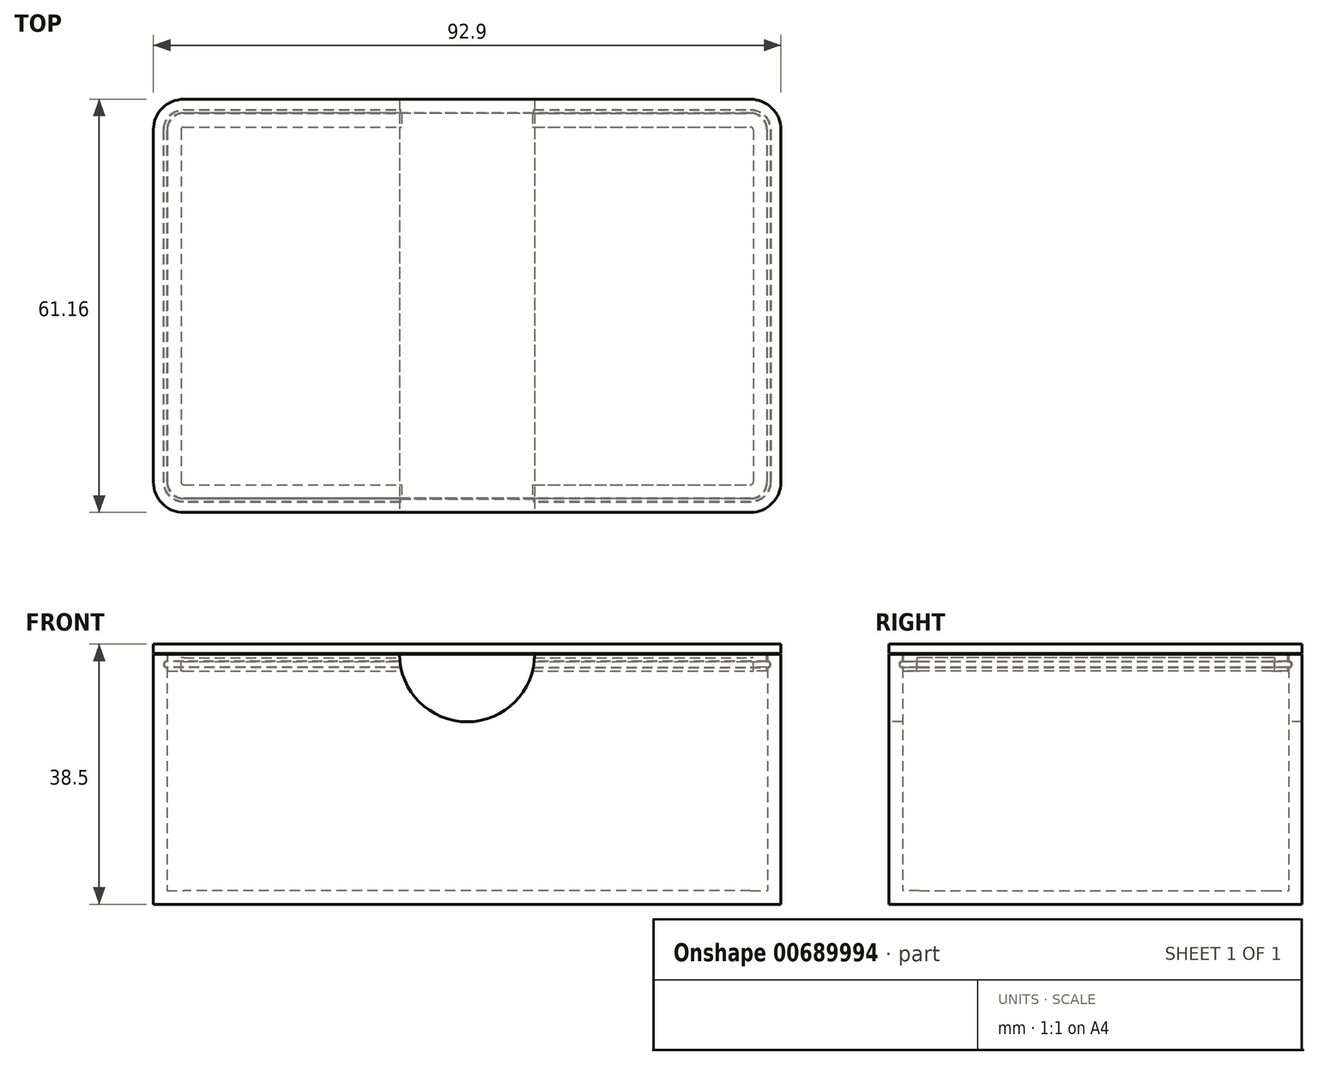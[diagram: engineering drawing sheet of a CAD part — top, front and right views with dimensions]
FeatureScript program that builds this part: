
annotation { "Feature Type Name" : "Feature", "Feature Type Description" : "" }
export const myFeature = defineFeature(function(context is Context, id is Id, definition is map)
    precondition{}
    {
        {
            assignVariable(context, id + "F0", {"name" : "thick", "anyValue" : 35 * mm});
        }
        {
            assignVariable(context, id + "F1", {"name" : "wall", "anyValue" : 2 * mm});
        }
        {
            var Q0;
            Q0=qCreatedBy(makeId("Top.planeOp"),FACE);
            var sketch = newSketch(context, id + "F2", { "sketchPlane" : qUnion([Q0])});
            skLineSegment(sketch, "E0.bottom", {"start": v(41.95, -28.57) * mm, "end": v(-41.95, -28.58) * mm});
            skLineSegment(sketch, "E0.top", {"start": v(41.95, 28.58) * mm, "end": v(-41.95, 28.57) * mm});
            skLineSegment(sketch, "E0.left", {"start": v(44.45, -26.07) * mm, "end": v(44.45, 26.08) * mm});
            skLineSegment(sketch, "E0.right", {"start": v(-44.45, -26.08) * mm, "end": v(-44.45, 26.07) * mm});
            skPoint(sketch, "E0.middle", {"position": v(0, 0) * mm});
            skPoint(sketch, "E1.visualSharp", {"position": v(-44.45, 28.57) * mm});
            skArc(sketch, "E1.filletArc", {"start": v(-41.95, 28.57) * mm, "mid": v(-43.72, 27.84) * mm, "end": v(-44.45, 26.07) * mm});
            skPoint(sketch, "E2.visualSharp", {"position": v(-44.45, -28.58) * mm});
            skArc(sketch, "E2.filletArc", {"start": v(-44.45, -26.08) * mm, "mid": v(-43.72, -27.84) * mm, "end": v(-41.95, -28.58) * mm});
            skPoint(sketch, "E3.visualSharp", {"position": v(44.45, -28.57) * mm});
            skArc(sketch, "E3.filletArc", {"start": v(41.95, -28.57) * mm, "mid": v(43.72, -27.84) * mm, "end": v(44.45, -26.07) * mm});
            skPoint(sketch, "E4.visualSharp", {"position": v(44.45, 28.58) * mm});
            skArc(sketch, "E4.filletArc", {"start": v(44.45, 26.08) * mm, "mid": v(43.72, 27.84) * mm, "end": v(41.95, 28.57) * mm});
            skSolve(sketch);
        }
        {
            var Q0;
            Q0=makeQuery(id+"F2.imprint","IMPRINT",FACE,{"disambiguationData":[TD([[makeQuery(id+"F2.imprint","IMPRINT",EDGE,{"derivedFrom":sQuery(id+"F2.wireOp",EDGE,"E0.bottom")}),-1.0]])]});
            extrude(context, id + "F3", {"entities" : qUnion([Q0]), "depth" : getVariable(context, 'thick'), "offsetDistance" : 25 * mm});
        }
        {
            var Q0;
            Q0=makeQuery(id+"F3.opExtrude","CAP_FACE",FACE,{"disambiguationData":[OSD([sQuery(id+"F2.wireOp",EDGE,"E0.bottom"),sQuery(id+"F2.wireOp",EDGE,"E0.top"),sQuery(id+"F2.wireOp",EDGE,"E0.left"),sQuery(id+"F2.wireOp",EDGE,"E0.right"),sQuery(id+"F2.wireOp",EDGE,"E1.filletArc"),sQuery(id+"F2.wireOp",EDGE,"E2.filletArc"),sQuery(id+"F2.wireOp",EDGE,"E3.filletArc"),sQuery(id+"F2.wireOp",EDGE,"E4.filletArc")])],"isStart":false});
            shell(context, id + "F4", {"entities" : qUnion([Q0]), "thickness" : getVariable(context, 'wall'), "oppositeDirection" : true});
        }
        {
            var Q0;
            Q0=makeQuery(id+"F3.opExtrude","CAP_FACE",FACE,{"disambiguationData":[OSD([sQuery(id+"F2.wireOp",EDGE,"E0.bottom"),sQuery(id+"F2.wireOp",EDGE,"E0.top"),sQuery(id+"F2.wireOp",EDGE,"E0.left"),sQuery(id+"F2.wireOp",EDGE,"E0.right"),sQuery(id+"F2.wireOp",EDGE,"E1.filletArc"),sQuery(id+"F2.wireOp",EDGE,"E2.filletArc"),sQuery(id+"F2.wireOp",EDGE,"E3.filletArc"),sQuery(id+"F2.wireOp",EDGE,"E4.filletArc")])],"isStart":false});
            cPlane(context, id + "F5", {"entities" : qUnion([Q0]), "cplaneType" : CPlaneType.OFFSET, "offset" : 1.5 * mm, "oppositeDirection" : true, "width" : 150 * mm, "height" : 150 * mm});
        }
        {
            var Q0;
            Q0=qCreatedBy(id+"F5.planeOp",FACE);
            var sketch = newSketch(context, id + "F6", { "sketchPlane" : qUnion([Q0])});
            skLineSegment(sketch, "E5.0", {"start": v(44.45, -26.07) * mm, "end": v(44.45, 26.08) * mm});
            skArc(sketch, "E5.1", {"start": v(41.95, -28.57) * mm, "mid": v(43.72, -27.84) * mm, "end": v(44.45, -26.07) * mm});
            skArc(sketch, "E5.2", {"start": v(44.45, 26.08) * mm, "mid": v(43.72, 27.84) * mm, "end": v(41.95, 28.57) * mm});
            skLineSegment(sketch, "E5.3", {"start": v(-41.95, -28.58) * mm, "end": v(41.95, -28.57) * mm});
            skLineSegment(sketch, "E5.4", {"start": v(41.95, 28.58) * mm, "end": v(-41.95, 28.57) * mm});
            skArc(sketch, "E5.5", {"start": v(-41.95, 28.57) * mm, "mid": v(-43.72, 27.84) * mm, "end": v(-44.45, 26.07) * mm});
            skLineSegment(sketch, "E5.6", {"start": v(-44.45, 26.07) * mm, "end": v(-44.45, -26.08) * mm});
            skArc(sketch, "E5.7", {"start": v(-44.45, -26.08) * mm, "mid": v(-43.72, -27.84) * mm, "end": v(-41.95, -28.58) * mm});
            skSolve(sketch);
        }
        {
            var Q0;
            Q0=qCreatedBy(makeId("Right.planeOp"),FACE);
            var sketch = newSketch(context, id + "F7", { "sketchPlane" : qUnion([Q0])});
            skCircle(sketch, "E6", {"center": v(28.57, 33.5) * mm, "radius": 0.5 * mm});
            skSolve(sketch);
        }
        {
            var Q0;
            Q0 = qSketchRegion(id + "F7", true);
            var Q1;
            Q1 = qConstructionFilter(qBodyType(qCreatedBy(id + "F6" ,EDGE), BodyType.WIRE), ConstructionObject.NO);
            sweep(context, id + "F8", {"operationType" : NewBodyOperationType.REMOVE, "profiles" : qUnion([Q0]), "path" : qUnion([Q1])});
        }
        {
            var Q0;
            Q0=qCreatedBy(id+"F5.planeOp",FACE);
            var sketch = newSketch(context, id + "F9", { "sketchPlane" : qUnion([Q0])});
            skLineSegment(sketch, "E7.0", {"start": v(41.95, 30.58) * mm, "end": v(-41.95, 30.58) * mm});
            skArc(sketch, "E7.1", {"start": v(46.45, 26.08) * mm, "mid": v(45.13, 29.26) * mm, "end": v(41.95, 30.57) * mm});
            skArc(sketch, "E7.2", {"start": v(-41.95, 30.57) * mm, "mid": v(-45.13, 29.26) * mm, "end": v(-46.45, 26.07) * mm});
            skLineSegment(sketch, "E7.3", {"start": v(46.45, -26.07) * mm, "end": v(46.45, 26.08) * mm});
            skLineSegment(sketch, "E7.4", {"start": v(-46.45, -26.08) * mm, "end": v(-46.45, 26.07) * mm});
            skArc(sketch, "E7.5", {"start": v(-46.45, -26.08) * mm, "mid": v(-45.13, -29.26) * mm, "end": v(-41.95, -30.58) * mm});
            skLineSegment(sketch, "E7.6", {"start": v(41.95, -30.58) * mm, "end": v(-41.95, -30.58) * mm});
            skArc(sketch, "E7.7", {"start": v(41.95, -30.57) * mm, "mid": v(45.13, -29.26) * mm, "end": v(46.45, -26.07) * mm});
            skSolve(sketch);
        }
        {
            var Q0;
            Q0 = qSketchRegion(id + "F9", true);
            extrude(context, id + "F10", {"entities" : qUnion([Q0]), "depth" : 3 * mm, "offsetDistance" : 25 * mm, "hasSecondDirection" : true, "secondDirectionOppositeDirection" : true, "secondDirectionDepth" : 1 * mm});
        }
        {
            var Q0;
            Q0=makeQuery(id+"F3.opExtrude","SWEPT_BODY",BODY,{"disambiguationData":[OSD([sQuery(id+"F2.wireOp",EDGE,"E0.bottom"),sQuery(id+"F2.wireOp",EDGE,"E0.top"),sQuery(id+"F2.wireOp",EDGE,"E0.left"),sQuery(id+"F2.wireOp",EDGE,"E0.right"),sQuery(id+"F2.wireOp",EDGE,"E1.filletArc"),sQuery(id+"F2.wireOp",EDGE,"E2.filletArc"),sQuery(id+"F2.wireOp",EDGE,"E3.filletArc"),sQuery(id+"F2.wireOp",EDGE,"E4.filletArc")])]});
            var Q1;
            Q1=makeQuery(id+"F10.opExtrude","SWEPT_BODY",BODY,{"disambiguationData":[OSD([sQuery(id+"F9.wireOp",EDGE,"E7.0"),sQuery(id+"F9.wireOp",EDGE,"E7.1"),sQuery(id+"F9.wireOp",EDGE,"E7.2"),sQuery(id+"F9.wireOp",EDGE,"E7.3"),sQuery(id+"F9.wireOp",EDGE,"E7.4"),sQuery(id+"F9.wireOp",EDGE,"E7.5"),sQuery(id+"F9.wireOp",EDGE,"E7.6"),sQuery(id+"F9.wireOp",EDGE,"E7.7")])]});
            booleanBodies(context, id + "F11", {"operationType" : BooleanOperationType.SUBTRACTION, "tools" : qUnion([Q0]), "targets" : qUnion([Q1]), "offset" : true, "offsetAll" : true, "offsetDistance" : 0.1 * mm, "keepTools" : true});
        }
        {
            var Q0;
            Q0=makeQuery(id+"F3.opExtrude","SWEPT_FACE",FACE,{"disambiguationData":[OSD([sQuery(id+"F2.wireOp",EDGE,"E0.bottom")])]});
            var sketch = newSketch(context, id + "F12", { "sketchPlane" : qUnion([Q0])});
            skCircle(sketch, "E8", {"center": v(0, 35) * mm, "radius": 10 * mm});
            skSolve(sketch);
        }
        {
            var Q0;
            {var subQ0=sQuery(id+"F12.wireOp",EDGE,"E8");var subQ1=makeQuery(id+"F3.opExtrude","CAP_EDGE",EDGE,{"disambiguationData":[OSD([sQuery(id+"F2.wireOp",EDGE,"E0.bottom")])],"isStart":false});var subQ2=makeQuery(id+"F12.imprint","INTERSECT",VERTEX,{"disambiguationData":[OD(0.0)],"derivedFrom":[subQ1,subQ0]});Q0=makeQuery(id+"F12.imprint","IMPRINT",FACE,{"disambiguationData":[TD([[makeQuery(id+"F12.imprint","IMPRINT",EDGE,{"disambiguationData":[TD([[subQ2,1.0]])],"derivedFrom":subQ0}),1.0]])]});}
            extrude(context, id + "F13", {"entities" : qUnion([Q0]), "operationType" : NewBodyOperationType.REMOVE, "endBound" : BoundingType.THROUGH_ALL, "oppositeDirection" : true, "depth" : 25 * mm, "offsetDistance" : 25 * mm});
        }
        {
            var Q0;
            Q0=makeQuery(id+"F10.opExtrude","CAP_FACE",FACE,{"disambiguationData":[OSD([sQuery(id+"F9.wireOp",EDGE,"E7.0"),sQuery(id+"F9.wireOp",EDGE,"E7.1"),sQuery(id+"F9.wireOp",EDGE,"E7.2"),sQuery(id+"F9.wireOp",EDGE,"E7.3"),sQuery(id+"F9.wireOp",EDGE,"E7.4"),sQuery(id+"F9.wireOp",EDGE,"E7.5"),sQuery(id+"F9.wireOp",EDGE,"E7.6"),sQuery(id+"F9.wireOp",EDGE,"E7.7")])],"isStart":true});
            var Q1;
            {var subQ0=sQuery(id+"F7.wireOp",EDGE,"E6");var subQ1=makeQuery(id+"F8.opSweep","SWEPT_FACE",FACE,{"disambiguationData":[OSD([sQuery(id+"F6.wireOp",EDGE,"E5.4"),subQ0])]});var subQ3=sQuery(id+"F2.wireOp",EDGE,"E3.filletArc");var subQ5=sQuery(id+"F2.wireOp",EDGE,"E2.filletArc");var subQ7=sQuery(id+"F2.wireOp",EDGE,"E4.filletArc");var subQ8=sQuery(id+"F2.wireOp",EDGE,"E1.filletArc");var subQ9=sQuery(id+"F2.wireOp",EDGE,"E0.right");var subQ10=sQuery(id+"F2.wireOp",EDGE,"E0.left");var subQ11=sQuery(id+"F2.wireOp",EDGE,"E0.top");var subQ12=sQuery(id+"F2.wireOp",EDGE,"E0.bottom");var subQ13=makeQuery(id+"F4.opShell","OFFSET_FACE",FACE,{"disambiguationData":[OSD([subQ12,subQ11,subQ10,subQ9,subQ8,subQ5,subQ3,subQ7])]});var subQ14=makeQuery(id+"F8.opSweep","SWEPT_FACE",FACE,{"disambiguationData":[OSD([sQuery(id+"F6.wireOp",EDGE,"E5.3"),subQ0])]});var subQ16=makeQuery(id+"F4.opShell","OFFSET_FACE",FACE,{"disambiguationData":[OSD([subQ12])]});var subQ21=makeQuery(id+"F4.opShell","OFFSET_FACE",FACE,{"disambiguationData":[OSD([subQ11])]});var subQ22=makeQuery(id+"F3.opExtrude","CAP_FACE",FACE,{"disambiguationData":[OSD([subQ12,subQ11,subQ10,subQ9,subQ8,subQ5,subQ3,subQ7])],"isStart":false});Q1=makeQuery(id+"F13.boolean.opBoolean","COPY",FACE,{"disambiguationData":[TD([makeQuery(id+"F10.opExtrude","CAP_FACE",FACE,{"disambiguationData":[OSD([sQuery(id+"F9.wireOp",EDGE,"E7.0"),sQuery(id+"F9.wireOp",EDGE,"E7.1"),sQuery(id+"F9.wireOp",EDGE,"E7.2"),sQuery(id+"F9.wireOp",EDGE,"E7.3"),sQuery(id+"F9.wireOp",EDGE,"E7.4"),sQuery(id+"F9.wireOp",EDGE,"E7.5"),sQuery(id+"F9.wireOp",EDGE,"E7.6"),sQuery(id+"F9.wireOp",EDGE,"E7.7")])],"isStart":true}),makeQuery(id+"F11.tempBoolean.opBoolean","COPY",FACE,{"derivedFrom":makeQuery(id+"F11.offsetTempBody.opPattern","COPY",FACE,{"derivedFrom":makeQuery(id+"F8.boolean.opBoolean","COPY",FACE,{"derivedFrom":subQ14}),"instanceName":"1"})}),makeQuery(id+"F11.tempBoolean.opBoolean","COPY",FACE,{"derivedFrom":makeQuery(id+"F11.offsetTempBody.opPattern","COPY",FACE,{"derivedFrom":makeQuery(id+"F8.boolean.opBoolean","COPY",FACE,{"derivedFrom":subQ1}),"instanceName":"1"})}),makeQuery(id+"F11.tempBoolean.opBoolean","COPY",FACE,{"derivedFrom":makeQuery(id+"F11.offsetTempBody.opPattern","COPY",FACE,{"derivedFrom":makeQuery(id+"F8.boolean.opBoolean","SPLIT",FACE,{"disambiguationData":[TD([subQ13])],"derivedFrom":subQ16}),"instanceName":"1"})}),makeQuery(id+"F11.tempBoolean.opBoolean","COPY",FACE,{"derivedFrom":makeQuery(id+"F11.offsetTempBody.opPattern","COPY",FACE,{"derivedFrom":makeQuery(id+"F8.boolean.opBoolean","SPLIT",FACE,{"disambiguationData":[TD([subQ22])],"derivedFrom":subQ16}),"instanceName":"1"})}),makeQuery(id+"F11.tempBoolean.opBoolean","COPY",FACE,{"derivedFrom":makeQuery(id+"F11.offsetTempBody.opPattern","COPY",FACE,{"derivedFrom":makeQuery(id+"F8.boolean.opBoolean","SPLIT",FACE,{"disambiguationData":[TD([subQ13])],"derivedFrom":subQ21}),"instanceName":"1"})}),makeQuery(id+"F11.tempBoolean.opBoolean","COPY",FACE,{"derivedFrom":makeQuery(id+"F11.offsetTempBody.opPattern","COPY",FACE,{"derivedFrom":makeQuery(id+"F8.boolean.opBoolean","SPLIT",FACE,{"disambiguationData":[TD([subQ22])],"derivedFrom":subQ21}),"instanceName":"1"})}),makeQuery(id+"F13.opExtrude","SWEPT_FACE",FACE,{"disambiguationData":[OSD([subQ12])]})]),OD(1.0)],"derivedFrom":makeQuery(id+"F13.opExtrude","SWEPT_FACE",FACE,{"disambiguationData":[OSD([sQuery(id+"F12.wireOp",EDGE,"E8")])]})});}
            var Q2;
            {var subQ0=sQuery(id+"F7.wireOp",EDGE,"E6");var subQ1=makeQuery(id+"F8.opSweep","SWEPT_FACE",FACE,{"disambiguationData":[OSD([sQuery(id+"F6.wireOp",EDGE,"E5.4"),subQ0])]});var subQ3=sQuery(id+"F2.wireOp",EDGE,"E3.filletArc");var subQ5=sQuery(id+"F2.wireOp",EDGE,"E2.filletArc");var subQ7=sQuery(id+"F2.wireOp",EDGE,"E4.filletArc");var subQ8=sQuery(id+"F2.wireOp",EDGE,"E1.filletArc");var subQ9=sQuery(id+"F2.wireOp",EDGE,"E0.right");var subQ10=sQuery(id+"F2.wireOp",EDGE,"E0.left");var subQ11=sQuery(id+"F2.wireOp",EDGE,"E0.top");var subQ12=sQuery(id+"F2.wireOp",EDGE,"E0.bottom");var subQ13=makeQuery(id+"F4.opShell","OFFSET_FACE",FACE,{"disambiguationData":[OSD([subQ12,subQ11,subQ10,subQ9,subQ8,subQ5,subQ3,subQ7])]});var subQ14=makeQuery(id+"F8.opSweep","SWEPT_FACE",FACE,{"disambiguationData":[OSD([sQuery(id+"F6.wireOp",EDGE,"E5.3"),subQ0])]});var subQ16=makeQuery(id+"F4.opShell","OFFSET_FACE",FACE,{"disambiguationData":[OSD([subQ12])]});var subQ21=makeQuery(id+"F4.opShell","OFFSET_FACE",FACE,{"disambiguationData":[OSD([subQ11])]});var subQ22=makeQuery(id+"F3.opExtrude","CAP_FACE",FACE,{"disambiguationData":[OSD([subQ12,subQ11,subQ10,subQ9,subQ8,subQ5,subQ3,subQ7])],"isStart":false});Q2=makeQuery(id+"F13.boolean.opBoolean","COPY",FACE,{"disambiguationData":[TD([makeQuery(id+"F10.opExtrude","CAP_FACE",FACE,{"disambiguationData":[OSD([sQuery(id+"F9.wireOp",EDGE,"E7.0"),sQuery(id+"F9.wireOp",EDGE,"E7.1"),sQuery(id+"F9.wireOp",EDGE,"E7.2"),sQuery(id+"F9.wireOp",EDGE,"E7.3"),sQuery(id+"F9.wireOp",EDGE,"E7.4"),sQuery(id+"F9.wireOp",EDGE,"E7.5"),sQuery(id+"F9.wireOp",EDGE,"E7.6"),sQuery(id+"F9.wireOp",EDGE,"E7.7")])],"isStart":true}),makeQuery(id+"F11.tempBoolean.opBoolean","COPY",FACE,{"derivedFrom":makeQuery(id+"F11.offsetTempBody.opPattern","COPY",FACE,{"derivedFrom":makeQuery(id+"F8.boolean.opBoolean","COPY",FACE,{"derivedFrom":subQ14}),"instanceName":"1"})}),makeQuery(id+"F11.tempBoolean.opBoolean","COPY",FACE,{"derivedFrom":makeQuery(id+"F11.offsetTempBody.opPattern","COPY",FACE,{"derivedFrom":makeQuery(id+"F8.boolean.opBoolean","COPY",FACE,{"derivedFrom":subQ1}),"instanceName":"1"})}),makeQuery(id+"F11.tempBoolean.opBoolean","COPY",FACE,{"derivedFrom":makeQuery(id+"F11.offsetTempBody.opPattern","COPY",FACE,{"derivedFrom":makeQuery(id+"F8.boolean.opBoolean","SPLIT",FACE,{"disambiguationData":[TD([subQ13])],"derivedFrom":subQ16}),"instanceName":"1"})}),makeQuery(id+"F11.tempBoolean.opBoolean","COPY",FACE,{"derivedFrom":makeQuery(id+"F11.offsetTempBody.opPattern","COPY",FACE,{"derivedFrom":makeQuery(id+"F8.boolean.opBoolean","SPLIT",FACE,{"disambiguationData":[TD([subQ22])],"derivedFrom":subQ16}),"instanceName":"1"})}),makeQuery(id+"F11.tempBoolean.opBoolean","COPY",FACE,{"derivedFrom":makeQuery(id+"F11.offsetTempBody.opPattern","COPY",FACE,{"derivedFrom":makeQuery(id+"F8.boolean.opBoolean","SPLIT",FACE,{"disambiguationData":[TD([subQ13])],"derivedFrom":subQ21}),"instanceName":"1"})}),makeQuery(id+"F11.tempBoolean.opBoolean","COPY",FACE,{"derivedFrom":makeQuery(id+"F11.offsetTempBody.opPattern","COPY",FACE,{"derivedFrom":makeQuery(id+"F8.boolean.opBoolean","SPLIT",FACE,{"disambiguationData":[TD([subQ22])],"derivedFrom":subQ21}),"instanceName":"1"})}),makeQuery(id+"F13.opExtrude","SWEPT_FACE",FACE,{"disambiguationData":[OSD([subQ12])]})]),OD(0.0)],"derivedFrom":makeQuery(id+"F13.opExtrude","SWEPT_FACE",FACE,{"disambiguationData":[OSD([sQuery(id+"F12.wireOp",EDGE,"E8")])]})});}
            shell(context, id + "F14", {"entities" : qUnion([Q0, Q1, Q2]), "thickness" : getVariable(context, 'wall')});
        }
    });
